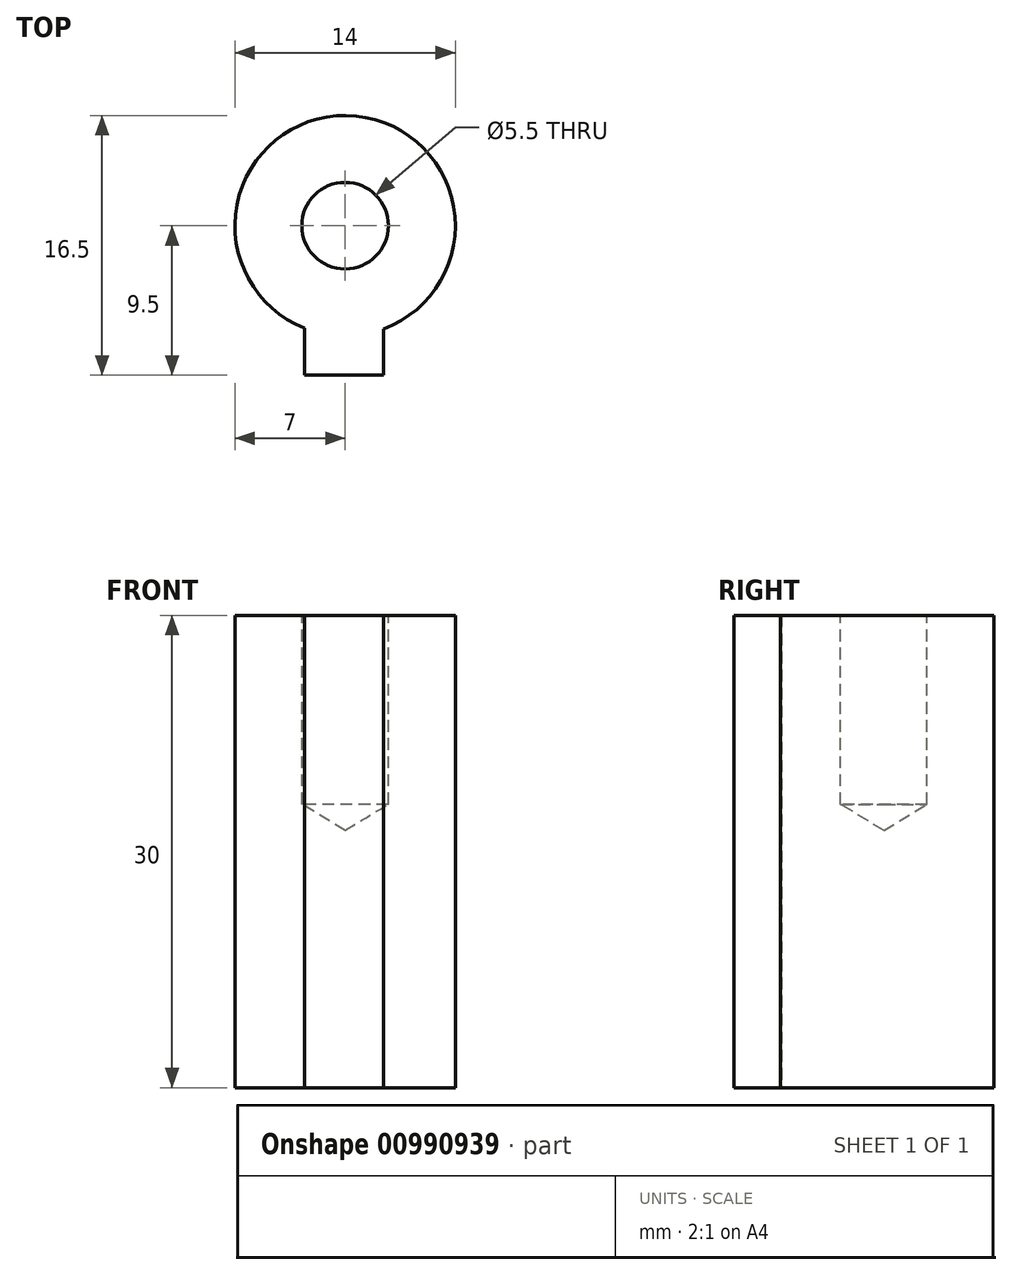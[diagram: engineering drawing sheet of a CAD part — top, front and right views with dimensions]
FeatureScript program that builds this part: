
annotation { "Feature Type Name" : "Feature", "Feature Type Description" : "" }
export const myFeature = defineFeature(function(context is Context, id is Id, definition is map)
    precondition{}
    {
        {
            var Q0;
            Q0=qCreatedBy(makeId("Top.planeOp"),FACE);
            var sketch = newSketch(context, id + "F0", { "sketchPlane" : qUnion([Q0])});
            skArc(sketch, "E0", {"start": v(2.44, -6.56) * mm, "mid": v(0.07, 7) * mm, "end": v(-2.56, -6.51) * mm});
            skLineSegment(sketch, "E1", {"start": v(-2.56, -6.51) * mm, "end": v(-2.56, -9.5) * mm});
            skLineSegment(sketch, "E2", {"start": v(-2.56, -9.5) * mm, "end": v(2.44, -9.5) * mm});
            skLineSegment(sketch, "E3", {"start": v(2.44, -9.5) * mm, "end": v(2.44, -6.56) * mm});
            skSolve(sketch);
        }
        {
            var Q0;
            Q0 = qSketchRegion(id + "F0", true);
            extrude(context, id + "F1", {"entities" : qUnion([Q0]), "depth" : 30 * mm, "offsetDistance" : 25 * mm});
        }
        {
            var Q0;
            Q0=makeQuery(id+"F1.opExtrude","CAP_FACE",FACE,{"disambiguationData":[OSD([sQuery(id+"F0.wireOp",EDGE,"E0"),sQuery(id+"F0.wireOp",EDGE,"E1"),sQuery(id+"F0.wireOp",EDGE,"E2"),sQuery(id+"F0.wireOp",EDGE,"E3")])],"isStart":false});
            var sketch = newSketch(context, id + "F2", { "sketchPlane" : qUnion([Q0])});
            skCircle(sketch, "E4", {"center": v(0, 0) * mm, "radius": 2.5 * mm});
            skSolve(sketch);
        }
        {
            var Q0;
            Q0=sQuery(id+"F2.wireOp",VERTEX,"E4.center");
            var Q1;
            Q1=makeQuery(id+"F1.opExtrude","SWEPT_BODY",BODY,{"disambiguationData":[OSD([sQuery(id+"F0.wireOp",EDGE,"E0"),sQuery(id+"F0.wireOp",EDGE,"E1"),sQuery(id+"F0.wireOp",EDGE,"E2"),sQuery(id+"F0.wireOp",EDGE,"E3")])]});
            hole(context, id + "F3", {"style" : HoleStyle.SIMPLE, "endStyle" : HoleEndStyle.BLIND, "standardTappedOrClearance" : lookupTablePath({ "fit" : "Normal", "standard" : "ISO", "size" : "M5", "type" : "Clearance" }), "standardBlindInLast" : lookupTablePath({ "fit" : "Normal", "standard" : "ISO", "engagement" : "75%", "pitch" : "0.8 mm", "size" : "M5", "type" : "Clearance & tapped" }), "holeDiameter" : 5.5 * mm, "majorDiameter" : 5 * mm, "holeDepth" : 12 * mm, "isTappedThrough" : true, "tappedDepth" : 12 * mm, "tapClearance" : 3, "locations" : qUnion([Q0]), "scope" : qUnion([Q1])});
        }
    });
